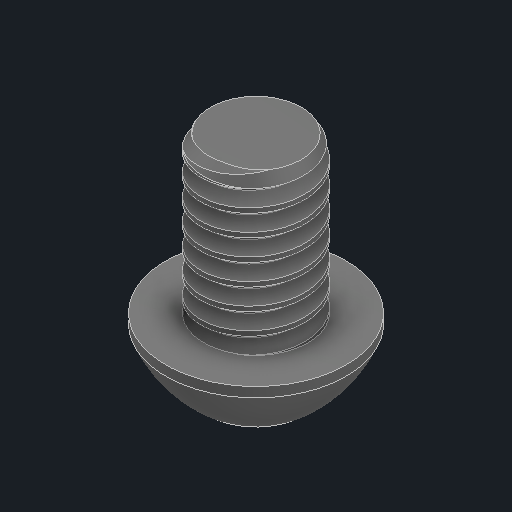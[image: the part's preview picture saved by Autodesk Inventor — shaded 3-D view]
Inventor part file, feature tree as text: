
AUTODESK INVENTOR PART (.ipt)
format: ipt  version: 2025 (Build 290162000, 162)  size: 308,224 bytes
history: native  units: in
note: dims shown in document units (in); Inventor stores cm internally (conversion verified against a paired STEP export)
features: thread x1
ambient origin geometry x8: Origin, YZ Plane, XZ Plane, XY Plane, X Axis, Y Axis, Z Axis, Center Point
bodies: Solid1 (feature_tree)
feature tree (1):
  thread  "THREADS"  [1 undecoded]
note: 1 required parameter value undecoded (feature->parameter linkage not recoverable at this tier; creation-order binding heuristic only, values carry confidence <= 0.55)
